# Revit family: 3455A_NX_Area_Controller
name_source: partatom
category: Communication Devices
units: mm (PartAtom-declared; Revit-internal decimal feet)

## family parameters
Cut with Voids When Loaded = No
Host = Face
Maintain Annotation Orientation = No
OmniClass Number = 23.85.80.11.27
OmniClass Title = Lighting Controls
Part Type = Normal
Room Calculation Point = No
Round Connector Dimension = Use Diameter
Shared = Yes

## types (1)
- 3455A_NX_Area_Controller
    Assembly Code = D5090
    Construction = NEMA1 metal enclosure
    Default Elevation = 48 "
    Description = The NX Area Controller provides a simple interface to the NX Distributed Intelligence™ Lighting Control Platform via a personal computer.
    Features = • Real-time programming and monitoring of the NX Distributed
Intelligence Lighting Control System
• No software required—built-in web server provides connection via any
Internet Explorer®-compatible browser
• Local or remote access via the local network or Internet
• Connect multiple users at once
• Integrates NX Lighting Control System and Building Automation
System (BAS) via BACnet IP
• Supports 128 areas, 128 zones per area
• NEMA enclosure with locking door
• Five-year limited warranty
• Delivers simplified configuration and control of  Lighting
luminaires using SpectraSync™ color tuning technology
    Handle = Metal-Nickel
    Height = 13.5 "
    Housing Material = Metal-Aluminum
    Manufacturer = NX Lighting Controls
    Model = NX Area Controller
    Operating Voltage = 120 V
    Type Comments = Area Controller
    URL = https://www.currentlighting.com
    Warranty = 5-Years Warranty
    Washer = Metal-Galvanized_Steel
    Width = 12 "

## geometry (parser evidence)
native form markers: Sweep x2
no freeform markers — native parametric forms only
